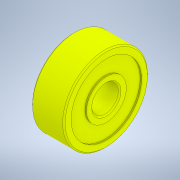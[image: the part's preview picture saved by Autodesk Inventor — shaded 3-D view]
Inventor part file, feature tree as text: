
AUTODESK INVENTOR PART (.ipt)
format: ipt  version: 2020 (Build 240168000, 168)  size: 154,624 bytes
history: native  units: mm
features: revolve x1, chamfer x1, sketch x1
ambient origin geometry x8: Origin, YZ Plane, XZ Plane, XY Plane, X Axis, Y Axis, Z Axis, Center Point
bodies: Solid1 (feature_tree)
feature tree (3):
  revolve  "Revolution1"  [1 undecoded]
  chamfer  "Chamfer1"  Distance=3.065mm
  sketch  "Sketch2"  dims[d0=5.0mm d1=2.05mm d2=3.065mm d3=5.4mm d4=6.5mm d5=0.2mm d6=90.0deg d7=0.2mm d8=2.0mm d9=45.0deg]
note: 1 required parameter value undecoded (feature->parameter linkage not recoverable at this tier; creation-order binding heuristic only, values carry confidence <= 0.55)
